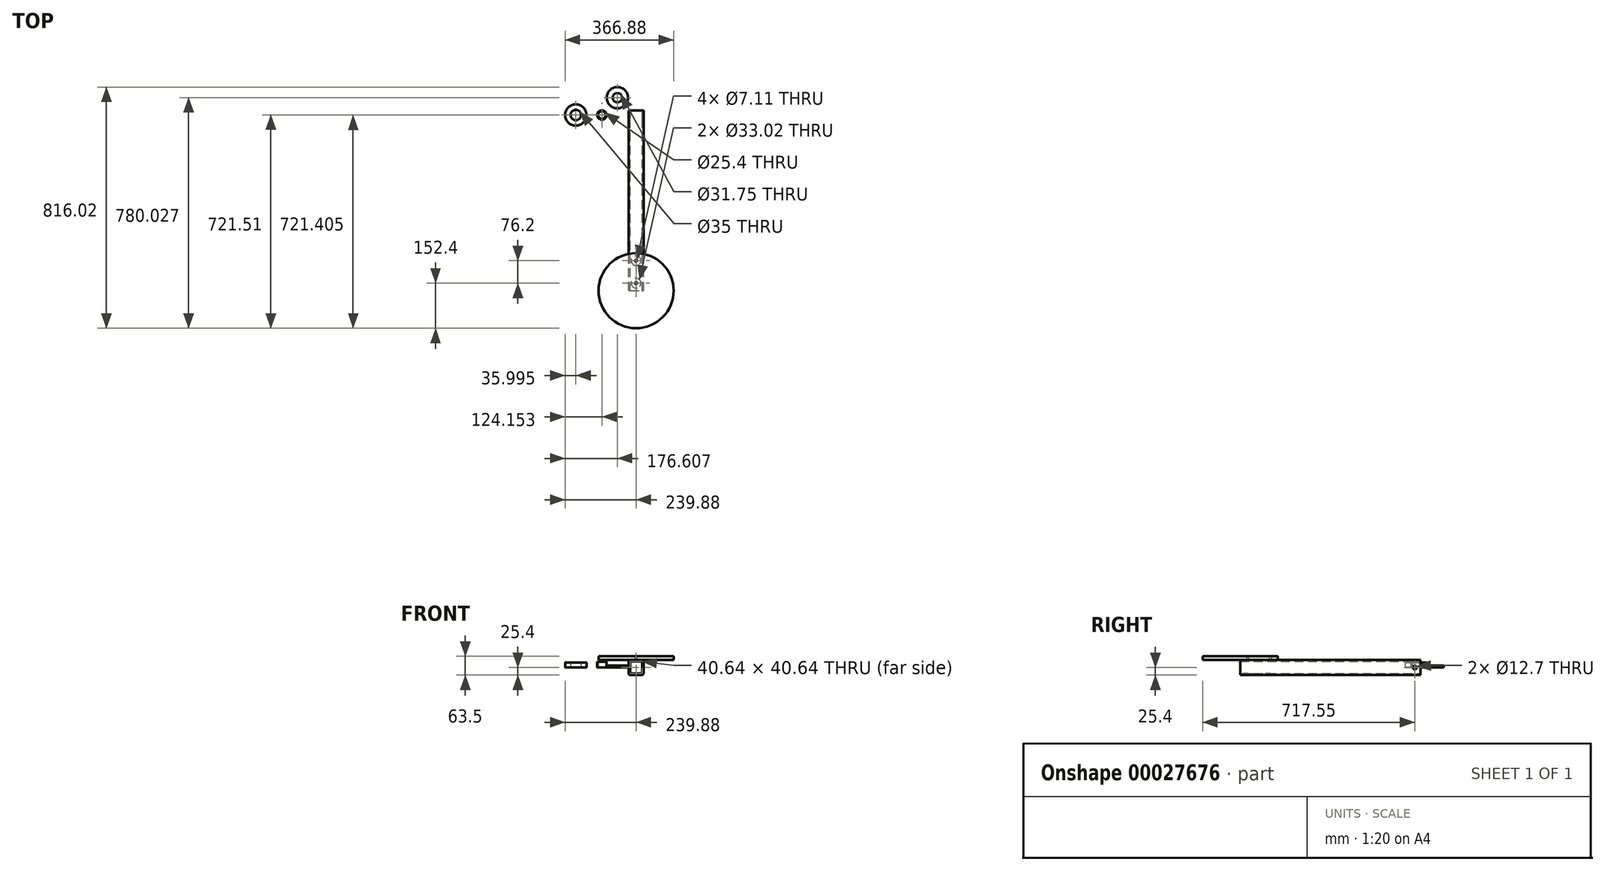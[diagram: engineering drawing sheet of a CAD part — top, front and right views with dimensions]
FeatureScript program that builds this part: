
annotation { "Feature Type Name" : "Feature", "Feature Type Description" : "" }
export const myFeature = defineFeature(function(context is Context, id is Id, definition is map)
    precondition{}
    {
        {
            var Q0;
            Q0=qCreatedBy(makeId("Front.planeOp"),FACE);
            var sketch = newSketch(context, id + "F0", { "sketchPlane" : qUnion([Q0])});
            skLineSegment(sketch, "E0.bottom", {"start": v(-19.05, 25.4) * mm, "end": v(19.05, 25.4) * mm});
            skLineSegment(sketch, "E0.top", {"start": v(-19.05, -25.4) * mm, "end": v(19.05, -25.4) * mm});
            skLineSegment(sketch, "E0.left", {"start": v(-25.4, 19.05) * mm, "end": v(-25.4, -19.05) * mm});
            skLineSegment(sketch, "E0.right", {"start": v(25.4, 19.05) * mm, "end": v(25.4, -19.05) * mm});
            skLineSegment(sketch, "E1", {"start": v(-25.4, 25.4) * mm, "end": v(25.4, -25.4) * mm, "construction": true});
            skPoint(sketch, "E2.visualSharp", {"position": v(-25.4, 25.4) * mm});
            skArc(sketch, "E2.filletArc", {"start": v(-19.05, 25.4) * mm, "mid": v(-23.54, 23.54) * mm, "end": v(-25.4, 19.05) * mm});
            skPoint(sketch, "E3.visualSharp", {"position": v(-25.4, -25.4) * mm});
            skArc(sketch, "E3.filletArc", {"start": v(-25.4, -19.05) * mm, "mid": v(-23.54, -23.54) * mm, "end": v(-19.05, -25.4) * mm});
            skPoint(sketch, "E4.visualSharp", {"position": v(25.4, -25.4) * mm});
            skArc(sketch, "E4.filletArc", {"start": v(19.05, -25.4) * mm, "mid": v(23.54, -23.54) * mm, "end": v(25.4, -19.05) * mm});
            skPoint(sketch, "E5.visualSharp", {"position": v(25.4, 25.4) * mm});
            skArc(sketch, "E5.filletArc", {"start": v(25.4, 19.05) * mm, "mid": v(23.54, 23.54) * mm, "end": v(19.05, 25.4) * mm});
            skLineSegment(sketch, "E6.0", {"start": v(-20.32, 20.32) * mm, "end": v(20.32, 20.32) * mm});
            skLineSegment(sketch, "E6.1", {"start": v(-20.32, 20.32) * mm, "end": v(-20.32, -20.32) * mm});
            skLineSegment(sketch, "E6.2", {"start": v(-20.32, -20.32) * mm, "end": v(20.32, -20.32) * mm});
            skLineSegment(sketch, "E6.3", {"start": v(20.32, 20.32) * mm, "end": v(20.32, -20.32) * mm});
            skSolve(sketch);
        }
        {
            var Q0;
            Q0 = qSketchRegion(id + "F0", true);
            extrude(context, id + "F1", {"entities" : qUnion([Q0]), "depth" : 609.6 * mm});
        }
        {
            var Q0;
            Q0=makeQuery(id+"F1.opExtrude","SWEPT_FACE",FACE,{"disambiguationData":[OSD([sQuery(id+"F0.wireOp",EDGE,"E0.bottom")])]});
            var sketch = newSketch(context, id + "F2", { "sketchPlane" : qUnion([Q0])});
            skCircle(sketch, "E7", {"center": v(0, -609.6) * mm, "radius": 127 * mm});
            skSolve(sketch);
        }
        {
            var Q0;
            Q0 = qSketchRegion(id + "F2", true);
            extrude(context, id + "F3", {"entities" : qUnion([Q0]), "depth" : 12.7 * mm});
        }
        {
            var Q0;
            Q0=makeQuery(id+"F1.opExtrude","SWEPT_FACE",FACE,{"disambiguationData":[OSD([sQuery(id+"F0.wireOp",EDGE,"E0.right")])]});
            var sketch = newSketch(context, id + "F4", { "sketchPlane" : qUnion([Q0])});
            skCircle(sketch, "E8", {"center": v(-19.05, 0) * mm, "radius": 6.35 * mm});
            skSolve(sketch);
        }
        {
            var Q0;
            Q0 = qSketchRegion(id + "F4", true);
            extrude(context, id + "F5", {"entities" : qUnion([Q0]), "operationType" : NewBodyOperationType.REMOVE, "endBound" : BoundingType.THROUGH_ALL, "oppositeDirection" : true, "depth" : 25.4 * mm});
        }
        {
            var Q0;
            Q0=qCreatedBy(makeId("Top.planeOp"),FACE);
            var sketch = newSketch(context, id + "F6", { "sketchPlane" : qUnion([Q0])});
            skCircle(sketch, "E9", {"center": v(-203.88, -15.09) * mm, "radius": 17.5 * mm});
            skCircle(sketch, "E10", {"center": v(-203.88, -15.09) * mm, "radius": 36 * mm});
            skSolve(sketch);
        }
        {
            var Q0;
            Q0=makeQuery(id+"F6.imprint","IMPRINT",FACE,{"disambiguationData":[TD([[makeQuery(id+"F6.imprint","IMPRINT",EDGE,{"derivedFrom":sQuery(id+"F6.wireOp",EDGE,"E9")}),-1.0]])]});
            extrude(context, id + "F7", {"entities" : qUnion([Q0]), "depth" : 17 * mm});
        }
        {
            var Q0;
            Q0=makeQuery(id+"F7.opExtrude","CAP_EDGE",EDGE,{"disambiguationData":[OSD([sQuery(id+"F6.wireOp",EDGE,"E10")])],"isStart":false});
            var Q1;
            Q1=makeQuery(id+"F7.opExtrude","CAP_EDGE",EDGE,{"disambiguationData":[OSD([sQuery(id+"F6.wireOp",EDGE,"E9")])],"isStart":false});
            var Q2;
            Q2=makeQuery(id+"F7.opExtrude","CAP_EDGE",EDGE,{"disambiguationData":[OSD([sQuery(id+"F6.wireOp",EDGE,"E10")])],"isStart":true});
            var Q3;
            Q3=makeQuery(id+"F7.opExtrude","CAP_EDGE",EDGE,{"disambiguationData":[OSD([sQuery(id+"F6.wireOp",EDGE,"E9")])],"isStart":true});
            fillet(context, id + "F8", {"entities" : qUnion([Q0, Q1, Q2, Q3]), "radius" : 1.27 * mm, "tangentPropagation" : true, "allowEdgeOverflow" : false});
        }
        {
            var Q0;
            Q0=qCreatedBy(makeId("Top.planeOp"),FACE);
            var sketch = newSketch(context, id + "F9", { "sketchPlane" : qUnion([Q0])});
            skCircle(sketch, "E11", {"center": v(-115.73, -15.2) * mm, "radius": 15.88 * mm});
            skCircle(sketch, "E12", {"center": v(-115.73, -15.2) * mm, "radius": 12.7 * mm});
            skSolve(sketch);
        }
        {
            var Q0;
            Q0=makeQuery(id+"F9.imprint","IMPRINT",FACE,{"disambiguationData":[TD([[makeQuery(id+"F9.imprint","IMPRINT",EDGE,{"derivedFrom":sQuery(id+"F9.wireOp",EDGE,"E11")}),1.0]])]});
            extrude(context, id + "F10", {"entities" : qUnion([Q0]), "depth" : 19.05 * mm});
        }
        {
            var Q0;
            Q0=makeQuery(id+"F10.opExtrude","CAP_EDGE",EDGE,{"disambiguationData":[OSD([sQuery(id+"F9.wireOp",EDGE,"E11")])],"isStart":false});
            var Q1;
            Q1=makeQuery(id+"F10.opExtrude","CAP_EDGE",EDGE,{"disambiguationData":[OSD([sQuery(id+"F9.wireOp",EDGE,"E11")])],"isStart":true});
            var Q2;
            Q2=makeQuery(id+"F10.opExtrude","CAP_EDGE",EDGE,{"disambiguationData":[OSD([sQuery(id+"F9.wireOp",EDGE,"E12")])],"isStart":false});
            var Q3;
            Q3=makeQuery(id+"F10.opExtrude","CAP_EDGE",EDGE,{"disambiguationData":[OSD([sQuery(id+"F9.wireOp",EDGE,"E12")])],"isStart":true});
            fillet(context, id + "F11", {"entities" : qUnion([Q0, Q1, Q2, Q3]), "radius" : 0.76 * mm, "tangentPropagation" : true, "allowEdgeOverflow" : false});
        }
        {
            var Q0;
            Q0=qCreatedBy(makeId("Top.planeOp"),FACE);
            var sketch = newSketch(context, id + "F12", { "sketchPlane" : qUnion([Q0])});
            skCircle(sketch, "E13", {"center": v(-63.27, 43.43) * mm, "radius": 36 * mm});
            skCircle(sketch, "E14", {"center": v(-63.27, 43.43) * mm, "radius": 15.88 * mm});
            skSolve(sketch);
        }
        {
            var Q0;
            Q0 = qSketchRegion(id + "F12", true);
            extrude(context, id + "F13", {"entities" : qUnion([Q0]), "depth" : 6.35 * mm});
        }
        {
            var Q0;
            Q0=makeQuery(id+"F13.opExtrude","CAP_FACE",FACE,{"disambiguationData":[OSD([sQuery(id+"F12.wireOp",EDGE,"E13"),sQuery(id+"F12.wireOp",EDGE,"E14")])],"isStart":false});
            var sketch = newSketch(context, id + "F14", { "sketchPlane" : qUnion([Q0])});
            skCircle(sketch, "E15", {"center": v(-63.27, 69.36) * mm, "radius": 8.26 * mm});
            skLineSegment(sketch, "E16", {"start": v(-63.27, 59.3) * mm, "end": v(-63.27, 79.42) * mm});
            skPoint(sketch, "E17", {"position": v(-63.27, 43.43) * mm});
            skCircle(sketch, "E18.1.0", {"center": v(-81.61, 61.76) * mm, "radius": 8.26 * mm});
            skCircle(sketch, "E18.2.0", {"center": v(-89.2, 43.43) * mm, "radius": 8.26 * mm});
            skCircle(sketch, "E18.3.0", {"center": v(-81.61, 25.09) * mm, "radius": 8.26 * mm});
            skCircle(sketch, "E18.4.0", {"center": v(-63.27, 17.5) * mm, "radius": 8.26 * mm});
            skCircle(sketch, "E18.5.0", {"center": v(-44.94, 25.09) * mm, "radius": 8.26 * mm});
            skCircle(sketch, "E18.6.0", {"center": v(-37.34, 43.43) * mm, "radius": 8.26 * mm});
            skCircle(sketch, "E18.7.0", {"center": v(-44.94, 61.76) * mm, "radius": 8.26 * mm});
            skSolve(sketch);
        }
        {
            var Q0;
            Q0=makeQuery(id+"F1.opExtrude","SWEPT_FACE",FACE,{"disambiguationData":[OSD([sQuery(id+"F0.wireOp",EDGE,"E0.top")])]});
            var sketch = newSketch(context, id + "F15", { "sketchPlane" : qUnion([Q0])});
            skCircle(sketch, "E19", {"center": v(0, 584.2) * mm, "radius": 16.51 * mm});
            skPoint(sketch, "E19.centerSnap0", {"position": v(0, 609.6) * mm});
            skCircle(sketch, "E20", {"center": v(0, 508) * mm, "radius": 16.51 * mm});
            skCircle(sketch, "E21", {"center": v(0, 508) * mm, "radius": 3.56 * mm});
            skCircle(sketch, "E22", {"center": v(0, 584.2) * mm, "radius": 3.56 * mm});
            skSolve(sketch);
        }
        {
            var Q0;
            Q0=makeQuery(id+"F15.imprint","IMPRINT",FACE,{"disambiguationData":[TD([[makeQuery(id+"F15.imprint","IMPRINT",EDGE,{"derivedFrom":sQuery(id+"F15.wireOp",EDGE,"E21")}),1.0]])]});
            var Q1;
            Q1=makeQuery(id+"F15.imprint","IMPRINT",FACE,{"disambiguationData":[TD([[makeQuery(id+"F15.imprint","IMPRINT",EDGE,{"derivedFrom":sQuery(id+"F15.wireOp",EDGE,"E22")}),1.0]])]});
            var Q2;
            Q2=makeQuery(id+"F15.imprint","IMPRINT",FACE,{"disambiguationData":[TD([[makeQuery(id+"F15.imprint","IMPRINT",EDGE,{"derivedFrom":sQuery(id+"F15.wireOp",EDGE,"E19")}),1.0]])]});
            var Q3;
            Q3=makeQuery(id+"F15.imprint","IMPRINT",FACE,{"disambiguationData":[TD([[makeQuery(id+"F15.imprint","IMPRINT",EDGE,{"derivedFrom":sQuery(id+"F15.wireOp",EDGE,"E20")}),1.0]])]});
            extrude(context, id + "F16", {"entities" : qUnion([Q0, Q1, Q2, Q3]), "operationType" : NewBodyOperationType.REMOVE, "oppositeDirection" : true, "depth" : 25.4 * mm});
        }
        {
            var Q0;
            Q0=makeQuery(id+"F15.imprint","IMPRINT",FACE,{"disambiguationData":[TD([[makeQuery(id+"F15.imprint","IMPRINT",EDGE,{"derivedFrom":sQuery(id+"F15.wireOp",EDGE,"E21")}),1.0]])]});
            var Q1;
            Q1=makeQuery(id+"F15.imprint","IMPRINT",FACE,{"disambiguationData":[TD([[makeQuery(id+"F15.imprint","IMPRINT",EDGE,{"derivedFrom":sQuery(id+"F15.wireOp",EDGE,"E22")}),1.0]])]});
            extrude(context, id + "F17", {"entities" : qUnion([Q0, Q1]), "operationType" : NewBodyOperationType.REMOVE, "endBound" : BoundingType.THROUGH_ALL, "oppositeDirection" : true, "depth" : 25.4 * mm});
        }
    });
